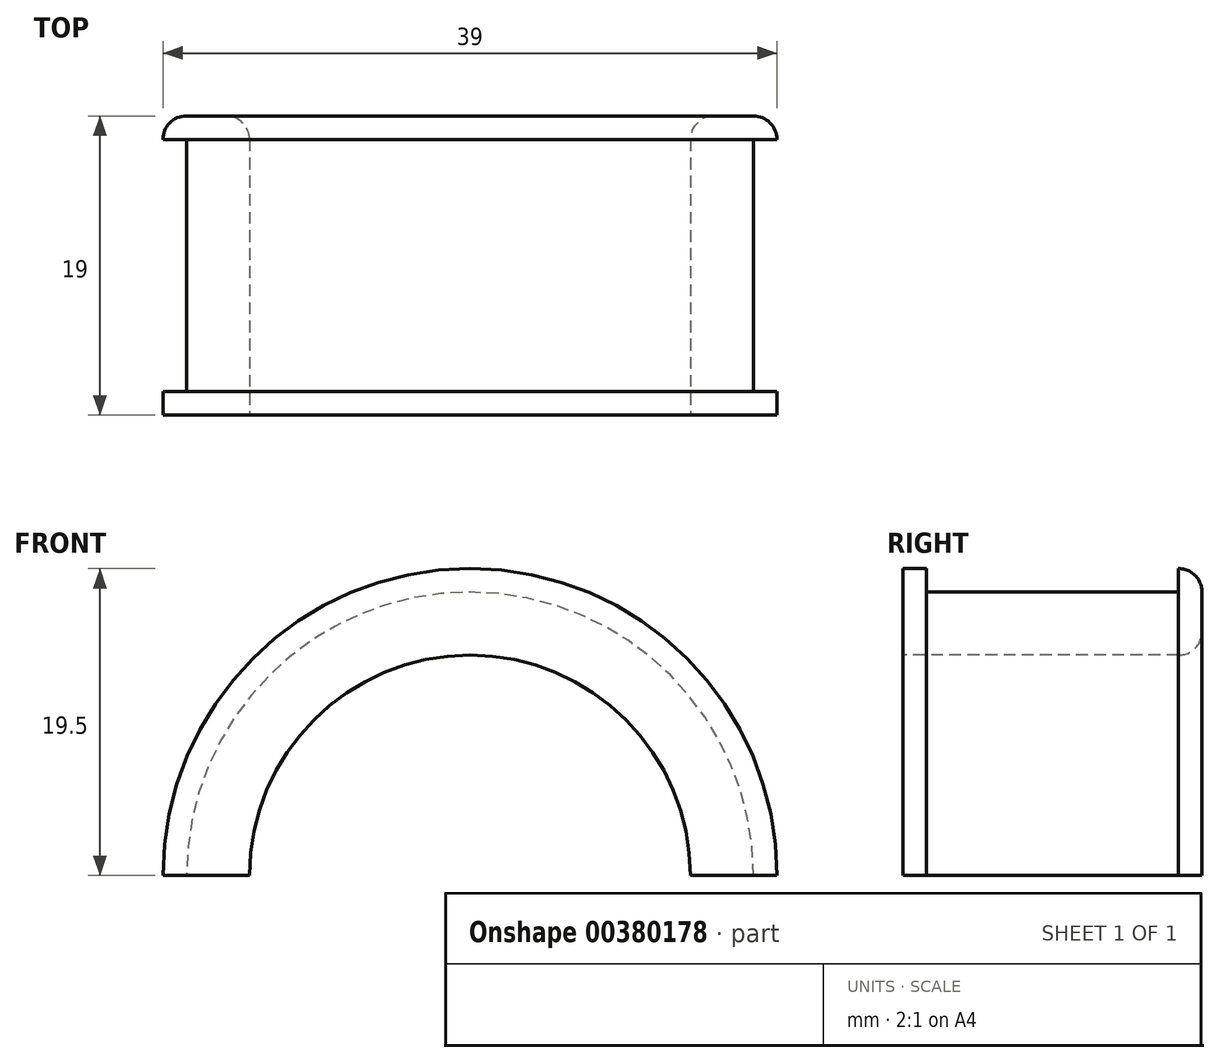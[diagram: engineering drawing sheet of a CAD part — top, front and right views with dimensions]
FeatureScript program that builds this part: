
annotation { "Feature Type Name" : "Feature", "Feature Type Description" : "" }
export const myFeature = defineFeature(function(context is Context, id is Id, definition is map)
    precondition{}
    {
        {
            var Q0;
            Q0=qCreatedBy(makeId("Top.planeOp"),FACE);
            var sketch = newSketch(context, id + "F0", { "sketchPlane" : qUnion([Q0])});
            skLineSegment(sketch, "E0.bottom", {"start": v(-18, 8) * mm, "end": v(18, 8) * mm});
            skLineSegment(sketch, "E0.top", {"start": v(-18, -8) * mm, "end": v(18, -8) * mm});
            skLineSegment(sketch, "E0.left", {"start": v(-18, 8) * mm, "end": v(-18, -8) * mm});
            skLineSegment(sketch, "E0.right", {"start": v(18, 8) * mm, "end": v(18, -8) * mm});
            skLineSegment(sketch, "E1.bottom", {"start": v(-19.5, 8) * mm, "end": v(19.5, 8) * mm});
            skLineSegment(sketch, "E1.top", {"start": v(-19.5, 9.5) * mm, "end": v(19.5, 9.5) * mm});
            skLineSegment(sketch, "E1.left", {"start": v(-19.5, 8) * mm, "end": v(-19.5, 9.5) * mm});
            skLineSegment(sketch, "E1.right", {"start": v(19.5, 8) * mm, "end": v(19.5, 9.5) * mm});
            skLineSegment(sketch, "E2.bottom", {"start": v(-19.5, -8) * mm, "end": v(19.5, -8) * mm});
            skLineSegment(sketch, "E2.top", {"start": v(-19.5, -9.5) * mm, "end": v(19.5, -9.5) * mm});
            skLineSegment(sketch, "E2.left", {"start": v(-19.5, -8) * mm, "end": v(-19.5, -9.5) * mm});
            skLineSegment(sketch, "E2.right", {"start": v(19.5, -8) * mm, "end": v(19.5, -9.5) * mm});
            skSolve(sketch);
        }
        {
            var Q0;
            {var subQ0=sQuery(id+"F0.wireOp",EDGE,"E0.left");Q0=makeQuery(id+"F0.imprint","IMPRINT",FACE,{"disambiguationData":[TD([[makeQuery(id+"F0.imprint","IMPRINT",EDGE,{"derivedFrom":subQ0}),1.0]])]});}
            extrude(context, id + "F1", {"entities" : qUnion([Q0]), "depth" : 18 * mm});
        }
        {
            var Q0;
            Q0=makeQuery(id+"F1.opExtrude","CAP_EDGE",EDGE,{"disambiguationData":[OSD([sQuery(id+"F0.wireOp",EDGE,"E0.right")])],"isStart":false});
            var Q1;
            Q1=makeQuery(id+"F1.opExtrude","CAP_EDGE",EDGE,{"disambiguationData":[OSD([sQuery(id+"F0.wireOp",EDGE,"E0.left")])],"isStart":false});
            fillet(context, id + "F2", {"entities" : qUnion([Q0, Q1]), "radius" : 18 * mm, "tangentPropagation" : true, "allowEdgeOverflow" : false});
        }
        {
            var Q0;
            Q0=makeQuery(id+"F0.imprint","IMPRINT",FACE,{"disambiguationData":[TD([[makeQuery(id+"F0.imprint","IMPRINT",EDGE,{"derivedFrom":sQuery(id+"F0.wireOp",EDGE,"E2.top")}),1.0]])]});
            var Q1;
            Q1=makeQuery(id+"F0.imprint","IMPRINT",FACE,{"disambiguationData":[TD([[makeQuery(id+"F0.imprint","IMPRINT",EDGE,{"derivedFrom":sQuery(id+"F0.wireOp",EDGE,"E1.top")}),-1.0]])]});
            extrude(context, id + "F3", {"entities" : qUnion([Q0, Q1]), "operationType" : NewBodyOperationType.ADD, "depth" : 19.5 * mm});
        }
        {
            var Q0;
            Q0=makeQuery(id+"F3.opExtrude","CAP_EDGE",EDGE,{"disambiguationData":[OSD([sQuery(id+"F0.wireOp",EDGE,"E2.right")])],"isStart":false});
            var Q1;
            Q1=makeQuery(id+"F3.opExtrude","CAP_EDGE",EDGE,{"disambiguationData":[OSD([sQuery(id+"F0.wireOp",EDGE,"E1.right")])],"isStart":false});
            var Q2;
            Q2=makeQuery(id+"F3.opExtrude","CAP_EDGE",EDGE,{"disambiguationData":[OSD([sQuery(id+"F0.wireOp",EDGE,"E2.left")])],"isStart":false});
            var Q3;
            Q3=makeQuery(id+"F3.opExtrude","CAP_EDGE",EDGE,{"disambiguationData":[OSD([sQuery(id+"F0.wireOp",EDGE,"E1.left")])],"isStart":false});
            fillet(context, id + "F4", {"entities" : qUnion([Q0, Q1, Q2, Q3]), "radius" : 19.5 * mm, "tangentPropagation" : true, "allowEdgeOverflow" : false});
        }
        {
            var Q0;
            Q0=makeQuery(id+"F3.opExtrude","SWEPT_FACE",FACE,{"disambiguationData":[OSD([sQuery(id+"F0.wireOp",EDGE,"E2.top")])]});
            var sketch = newSketch(context, id + "F5", { "sketchPlane" : qUnion([Q0])});
            skArc(sketch, "E3", {"start": v(14, 0) * mm, "mid": v(0, 14) * mm, "end": v(-14, 0) * mm});
            skSolve(sketch);
        }
        {
            var Q0;
            Q0=qSketchRegion(id+"F5",true);
            var Q1;
            {var subQ0=sQuery(id+"F5.wireOp",EDGE,"E3");Q1=makeQuery(id+"F5.imprint","IMPRINT",FACE,{"disambiguationData":[TD([[makeQuery(id+"F5.imprint","IMPRINT",EDGE,{"derivedFrom":subQ0}),1.0]])]});}
            extrude(context, id + "F6", {"entities" : qUnion([Q0, Q1]), "operationType" : NewBodyOperationType.REMOVE, "oppositeDirection" : true, "depth" : 25.4 * mm});
        }
        {
            var Q0;
            Q0=makeQuery(id+"F4.opFillet","BLEND_EDGE",EDGE,{"blendedFrom":[makeQuery(id+"F3.opExtrude","CAP_EDGE",EDGE,{"disambiguationData":[OSD([sQuery(id+"F0.wireOp",EDGE,"E2.right")])],"isStart":false}),makeQuery(id+"F3.opExtrude","SWEPT_FACE",FACE,{"disambiguationData":[OSD([sQuery(id+"F0.wireOp",EDGE,"E2.top")])]})],"blendedInto":[makeQuery(id+"F3.opExtrude","SWEPT_FACE",FACE,{"disambiguationData":[OSD([sQuery(id+"F0.wireOp",EDGE,"E2.top")])]})]});
            var Q1;
            Q1=makeQuery(id+"F4.opFillet","BLEND_EDGE",EDGE,{"blendedFrom":[makeQuery(id+"F3.opExtrude","CAP_EDGE",EDGE,{"disambiguationData":[OSD([sQuery(id+"F0.wireOp",EDGE,"E1.left")])],"isStart":false}),makeQuery(id+"F3.opExtrude","SWEPT_FACE",FACE,{"disambiguationData":[OSD([sQuery(id+"F0.wireOp",EDGE,"E1.top")])]})],"blendedInto":[makeQuery(id+"F3.opExtrude","SWEPT_FACE",FACE,{"disambiguationData":[OSD([sQuery(id+"F0.wireOp",EDGE,"E1.top")])]})]});
            var Q2;
            Q2=makeQuery(id+"F6.boolean.opBoolean","INTERSECT",EDGE,{"derivedFrom":[makeQuery(id+"F3.opExtrude","SWEPT_FACE",FACE,{"disambiguationData":[OSD([sQuery(id+"F0.wireOp",EDGE,"E1.top")])]}),makeQuery(id+"F6.opExtrude","SWEPT_FACE",FACE,{"disambiguationData":[OSD([sQuery(id+"F5.wireOp",EDGE,"E3")])]})]});
            var Q3;
            Q3=makeQuery(id+"F6.boolean.opBoolean","COPY",EDGE,{"derivedFrom":makeQuery(id+"F6.opExtrude","CAP_EDGE",EDGE,{"disambiguationData":[OSD([sQuery(id+"F5.wireOp",EDGE,"E3")])],"isStart":true})});
            fillet(context, id + "F7", {"entities" : qUnion([Q0, Q1, Q2, Q3]), "radius" : 1.5 * mm, "tangentPropagation" : true, "allowEdgeOverflow" : false});
        }
    });
